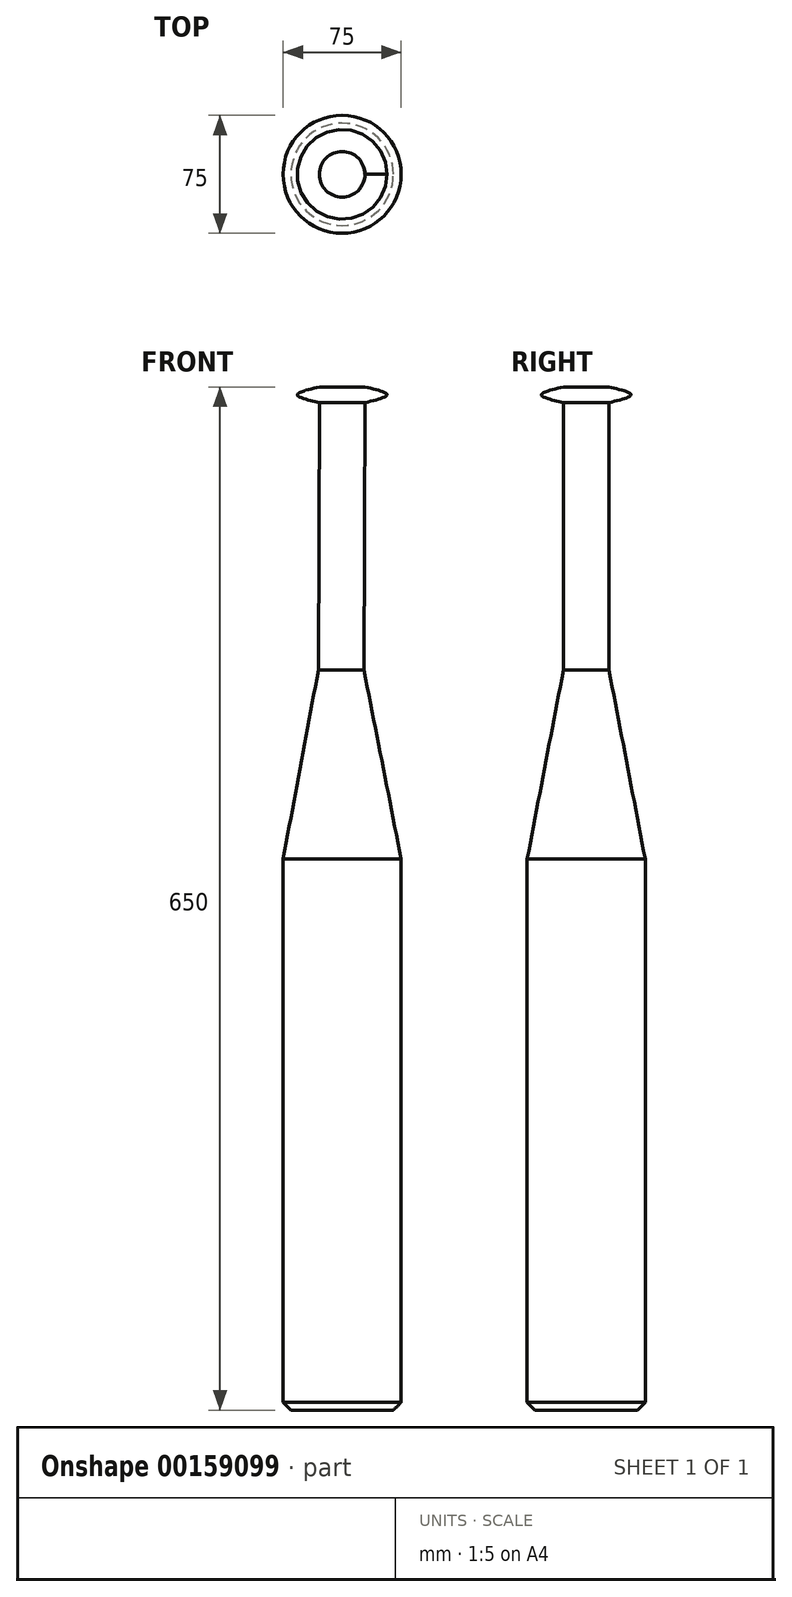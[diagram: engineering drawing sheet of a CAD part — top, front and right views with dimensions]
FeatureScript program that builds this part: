
annotation { "Feature Type Name" : "Feature", "Feature Type Description" : "" }
export const myFeature = defineFeature(function(context is Context, id is Id, definition is map)
    precondition{}
    {
        {
            var Q0;
            Q0=qCreatedBy(makeId("Top.planeOp"),FACE);
            cPlane(context, id + "F0", {"entities" : qUnion([Q0]), "cplaneType" : CPlaneType.OFFSET, "offset" : 300 * mm, "width" : 152.4 * mm, "height" : 152.4 * mm});
        }
        {
            var Q0;
            Q0=qCreatedBy(makeId("Top.planeOp"),FACE);
            cPlane(context, id + "F1", {"entities" : qUnion([Q0]), "cplaneType" : CPlaneType.OFFSET, "offset" : 295 * mm, "width" : 150 * mm, "height" : 150 * mm});
        }
        {
            var Q0;
            Q0=qCreatedBy(makeId("Top.planeOp"),FACE);
            cPlane(context, id + "F2", {"entities" : qUnion([Q0]), "cplaneType" : CPlaneType.OFFSET, "offset" : 290 * mm, "width" : 150 * mm, "height" : 150 * mm});
        }
        {
            var Q0;
            Q0=qCreatedBy(makeId("Top.planeOp"),FACE);
            cPlane(context, id + "F3", {"entities" : qUnion([Q0]), "cplaneType" : CPlaneType.OFFSET, "offset" : 350 * mm, "oppositeDirection" : true, "width" : 150 * mm, "height" : 150 * mm});
        }
        {
            var Q0;
            Q0=qCreatedBy(id+"F3.planeOp",FACE);
            cPlane(context, id + "F4", {"entities" : qUnion([Q0]), "cplaneType" : CPlaneType.OFFSET, "offset" : 5 * mm, "width" : 150 * mm, "height" : 150 * mm});
        }
        {
            var Q0;
            Q0=qCreatedBy(id+"F3.planeOp",FACE);
            var sketch = newSketch(context, id + "F5", { "sketchPlane" : qUnion([Q0])});
            skCircle(sketch, "E0", {"center": v(0, 0) * mm, "radius": 32.5 * mm});
            skSolve(sketch);
        }
        {
            var Q0;
            Q0=qCreatedBy(id+"F4.planeOp",FACE);
            var sketch = newSketch(context, id + "F6", { "sketchPlane" : qUnion([Q0])});
            skCircle(sketch, "E1", {"center": v(0, 0) * mm, "radius": 37.5 * mm});
            skSolve(sketch);
        }
        {
            var Q0;
            Q0=qSketchRegion(id+"F5",true);
            var Q1;
            Q1=qSketchRegion(id+"F6",true);
            loft(context, id + "F7", {"sheetProfilesArray" : [{ "sheetProfileEntities" : qUnion([Q0]) }, { "sheetProfileEntities" : qUnion([Q1]) }]});
        }
        {
            var Q0;
            Q0=qCreatedBy(makeId("Top.planeOp"),FACE);
            var sketch = newSketch(context, id + "F8", { "sketchPlane" : qUnion([Q0])});
            skCircle(sketch, "E2", {"center": v(0, 0) * mm, "radius": 37.5 * mm});
            skSolve(sketch);
        }
        {
            var Q1;
            Q1=qSketchRegion(id+"F8",true);
            var Q2;
            Q2=qSketchRegion(id+"F6",true);
            loft(context, id + "F9", {"operationType" : NewBodyOperationType.ADD, "sheetProfilesArray" : [{ "sheetProfileEntities" : qUnion([Q1]) }, { "sheetProfileEntities" : qUnion([Q2]) }]});
        }
        {
            var Q0;
            Q0=qCreatedBy(makeId("Top.planeOp"),FACE);
            cPlane(context, id + "F10", {"entities" : qUnion([Q0]), "cplaneType" : CPlaneType.OFFSET, "offset" : 120 * mm, "width" : 150 * mm, "height" : 150 * mm});
        }
        {
            var Q0;
            Q0=qCreatedBy(id+"F10.planeOp",FACE);
            var sketch = newSketch(context, id + "F11", { "sketchPlane" : qUnion([Q0])});
            skCircle(sketch, "E3", {"center": v(-0.64, 0) * mm, "radius": 14.5 * mm});
            skSolve(sketch);
        }
        {
            var Q0;
            Q0=qSketchRegion(id+"F8",true);
            var Q1;
            Q1=qSketchRegion(id+"F11",true);
            loft(context, id + "F12", {"sheetProfilesArray" : [{ "sheetProfileEntities" : qUnion([Q0]) }, { "sheetProfileEntities" : qUnion([Q1]) }]});
        }
        {
            var Q0;
            Q0=qCreatedBy(id+"F2.planeOp",FACE);
            var sketch = newSketch(context, id + "F13", { "sketchPlane" : qUnion([Q0])});
            skCircle(sketch, "E4", {"center": v(0, 0) * mm, "radius": 14.5 * mm});
            skSolve(sketch);
        }
        {
            var Q0;
            Q0=qSketchRegion(id+"F11",true);
            var Q1;
            Q1=qSketchRegion(id+"F13",true);
            loft(context, id + "F14", {"sheetProfilesArray" : [{ "sheetProfileEntities" : qUnion([Q0]) }, { "sheetProfileEntities" : qUnion([Q1]) }]});
        }
        {
            var Q0;
            Q0=qCreatedBy(id+"F1.planeOp",FACE);
            var sketch = newSketch(context, id + "F15", { "sketchPlane" : qUnion([Q0])});
            skCircle(sketch, "E5", {"center": v(0, 0) * mm, "radius": 28.5 * mm});
            skSolve(sketch);
        }
        {
            var Q0;
            Q0=qCreatedBy(id+"F0.planeOp",FACE);
            var sketch = newSketch(context, id + "F16", { "sketchPlane" : qUnion([Q0])});
            skCircle(sketch, "E6", {"center": v(0, 0) * mm, "radius": 14.5 * mm});
            skSolve(sketch);
        }
        {
            var Q0;
            Q0=qSketchRegion(id+"F13",true);
            var Q1;
            Q1=qSketchRegion(id+"F15",true);
            var Q2;
            Q2=qSketchRegion(id+"F16",true);
            loft(context, id + "F17", {"sheetProfilesArray" : [{ "sheetProfileEntities" : qUnion([Q0]) }, { "sheetProfileEntities" : qUnion([Q1]) }, { "sheetProfileEntities" : qUnion([Q2]) }]});
        }
    });
